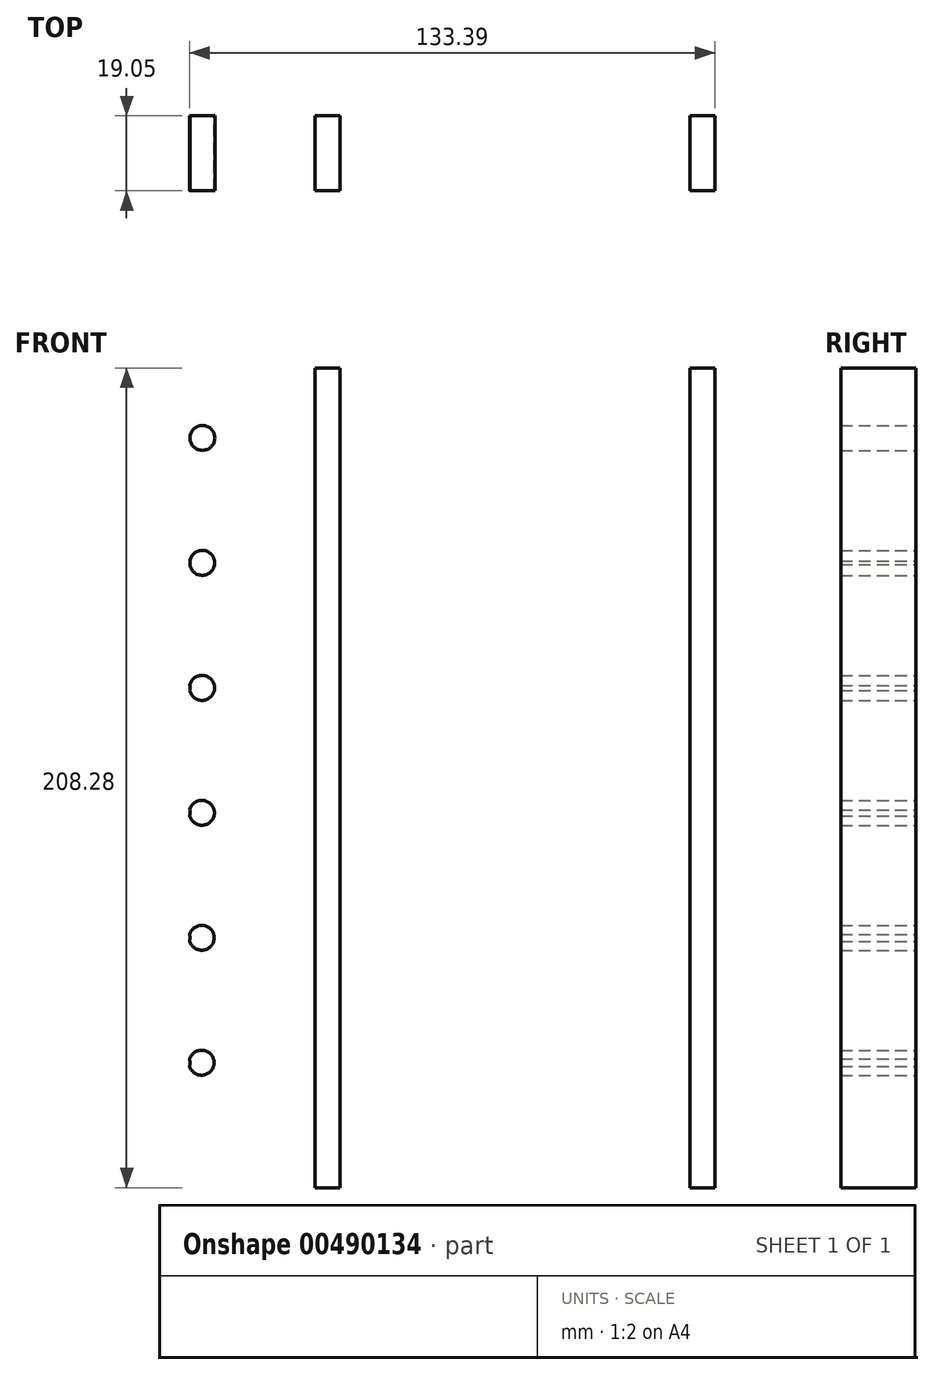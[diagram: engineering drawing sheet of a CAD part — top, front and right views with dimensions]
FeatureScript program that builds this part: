
annotation { "Feature Type Name" : "Feature", "Feature Type Description" : "" }
export const myFeature = defineFeature(function(context is Context, id is Id, definition is map)
    precondition{}
    {
        {
            var Q0;
            Q0=qCreatedBy(makeId("Front.planeOp"),FACE);
            var sketch = newSketch(context, id + "F0", { "sketchPlane" : qUnion([Q0])});
            skCircle(sketch, "E0", {"center": v(63.67, 62.96) * mm, "radius": 12.7 * mm});
            skCircle(sketch, "E1", {"center": v(95.42, 62.96) * mm, "radius": 12.7 * mm});
            skCircle(sketch, "E2", {"center": v(0.17, 62.96) * mm, "radius": 12.7 * mm});
            skCircle(sketch, "E3", {"center": v(31.92, 62.96) * mm, "radius": 12.7 * mm});
            skCircle(sketch, "E4", {"center": v(-31.58, 62.96) * mm, "radius": 12.7 * mm});
            skCircle(sketch, "E5", {"center": v(-63.33, 62.96) * mm, "radius": 12.7 * mm});
            skCircle(sketch, "E6", {"center": v(-95.08, 62.96) * mm, "radius": 12.7 * mm});
            skCircle(sketch, "E7", {"center": v(63.67, -32.3) * mm, "radius": 12.7 * mm});
            skCircle(sketch, "E8", {"center": v(95.42, -32.3) * mm, "radius": 12.7 * mm});
            skCircle(sketch, "E9", {"center": v(0.17, -32.3) * mm, "radius": 12.7 * mm});
            skCircle(sketch, "E10", {"center": v(31.92, -32.3) * mm, "radius": 12.7 * mm});
            skCircle(sketch, "E11", {"center": v(-31.58, -32.3) * mm, "radius": 12.7 * mm});
            skCircle(sketch, "E12", {"center": v(-63.33, -32.3) * mm, "radius": 12.7 * mm});
            skCircle(sketch, "E13", {"center": v(-95.08, -32.3) * mm, "radius": 12.7 * mm});
            skCircle(sketch, "E14", {"center": v(63.67, 31.2) * mm, "radius": 12.7 * mm});
            skCircle(sketch, "E15", {"center": v(95.42, 31.2) * mm, "radius": 12.7 * mm});
            skCircle(sketch, "E16", {"center": v(0.17, 31.2) * mm, "radius": 12.7 * mm});
            skCircle(sketch, "E17", {"center": v(31.92, 31.2) * mm, "radius": 12.7 * mm});
            skCircle(sketch, "E18", {"center": v(-31.58, 31.2) * mm, "radius": 12.7 * mm});
            skCircle(sketch, "E19", {"center": v(-63.33, 31.2) * mm, "radius": 12.7 * mm});
            skCircle(sketch, "E20", {"center": v(-95.08, 31.2) * mm, "radius": 12.7 * mm});
            skCircle(sketch, "E21", {"center": v(63.67, -0.54) * mm, "radius": 12.7 * mm});
            skCircle(sketch, "E22", {"center": v(95.42, -0.54) * mm, "radius": 12.7 * mm});
            skCircle(sketch, "E23", {"center": v(0.17, -0.54) * mm, "radius": 12.7 * mm});
            skCircle(sketch, "E24", {"center": v(31.92, -0.54) * mm, "radius": 12.7 * mm});
            skCircle(sketch, "E25", {"center": v(-31.58, -0.54) * mm, "radius": 12.7 * mm});
            skCircle(sketch, "E26", {"center": v(-63.33, -0.54) * mm, "radius": 12.7 * mm});
            skCircle(sketch, "E27", {"center": v(-95.08, -0.54) * mm, "radius": 12.7 * mm});
            skCircle(sketch, "E28", {"center": v(63.67, -64.04) * mm, "radius": 12.7 * mm});
            skCircle(sketch, "E29", {"center": v(95.42, -64.04) * mm, "radius": 12.7 * mm});
            skCircle(sketch, "E30", {"center": v(0.17, -64.04) * mm, "radius": 12.7 * mm});
            skCircle(sketch, "E31", {"center": v(31.92, -64.04) * mm, "radius": 12.7 * mm});
            skCircle(sketch, "E32", {"center": v(-31.58, -64.04) * mm, "radius": 12.7 * mm});
            skCircle(sketch, "E33", {"center": v(-63.33, -64.04) * mm, "radius": 12.7 * mm});
            skCircle(sketch, "E34", {"center": v(-95.08, -64.04) * mm, "radius": 12.7 * mm});
            skCircle(sketch, "E35", {"center": v(63.67, -95.8) * mm, "radius": 12.7 * mm});
            skCircle(sketch, "E36", {"center": v(95.42, -95.8) * mm, "radius": 12.7 * mm});
            skCircle(sketch, "E37", {"center": v(0.17, -95.8) * mm, "radius": 12.7 * mm});
            skCircle(sketch, "E38", {"center": v(31.92, -95.8) * mm, "radius": 12.7 * mm});
            skCircle(sketch, "E39", {"center": v(-31.58, -95.8) * mm, "radius": 12.7 * mm});
            skCircle(sketch, "E40", {"center": v(-63.33, -95.8) * mm, "radius": 12.7 * mm});
            skCircle(sketch, "E41", {"center": v(-95.08, -95.8) * mm, "radius": 12.7 * mm});
            skLineSegment(sketch, "E42.bottom", {"start": v(-115.4, 82) * mm, "end": v(115.74, 82) * mm});
            skLineSegment(sketch, "E42.top", {"start": v(-115.4, -127.54) * mm, "end": v(115.74, -127.54) * mm});
            skLineSegment(sketch, "E42.left", {"start": v(-115.4, 82) * mm, "end": v(-115.4, -127.54) * mm});
            skLineSegment(sketch, "E42.right", {"start": v(115.74, 82) * mm, "end": v(115.74, -127.54) * mm});
            skLineSegment(sketch, "E43.bottom", {"start": v(-115.4, 82) * mm, "end": v(-107.78, 82) * mm});
            skLineSegment(sketch, "E43.top", {"start": v(-115.4, -127.54) * mm, "end": v(-107.78, -127.54) * mm});
            skLineSegment(sketch, "E43.right", {"start": v(-107.78, 82) * mm, "end": v(-107.78, -127.54) * mm});
            skLineSegment(sketch, "E44.bottom", {"start": v(115.74, 82) * mm, "end": v(108.12, 82) * mm});
            skLineSegment(sketch, "E44.top", {"start": v(115.74, -127.54) * mm, "end": v(108.12, -127.54) * mm});
            skLineSegment(sketch, "E44.right", {"start": v(108.12, 82) * mm, "end": v(108.12, -127.54) * mm});
            skLineSegment(sketch, "E45.top", {"start": v(76.37, -127.54) * mm, "end": v(82.72, -127.54) * mm});
            skLineSegment(sketch, "E46.bottom", {"start": v(44.62, 80.74) * mm, "end": v(50.97, 80.74) * mm});
            skLineSegment(sketch, "E46.top", {"start": v(44.62, -127.54) * mm, "end": v(50.97, -127.54) * mm});
            skLineSegment(sketch, "E46.left", {"start": v(44.62, 80.74) * mm, "end": v(44.62, -127.54) * mm});
            skLineSegment(sketch, "E46.right", {"start": v(50.97, 80.74) * mm, "end": v(50.97, -127.54) * mm});
            skLineSegment(sketch, "E47.bottom", {"start": v(-50.63, 80.74) * mm, "end": v(-44.28, 80.74) * mm});
            skLineSegment(sketch, "E47.top", {"start": v(-50.63, -127.54) * mm, "end": v(-44.28, -127.54) * mm});
            skLineSegment(sketch, "E47.left", {"start": v(-50.63, 80.74) * mm, "end": v(-50.63, -127.54) * mm});
            skLineSegment(sketch, "E47.right", {"start": v(-44.28, 80.74) * mm, "end": v(-44.28, -127.54) * mm});
            skCircle(sketch, "E48", {"center": v(-79.2, 62.96) * mm, "radius": 3.18 * mm});
            skCircle(sketch, "E49.1.0.0", {"center": v(-79.25, 31.2) * mm, "radius": 3.18 * mm});
            skCircle(sketch, "E49.2.0.0", {"center": v(-79.29, -0.54) * mm, "radius": 3.18 * mm});
            skCircle(sketch, "E49.3.0.0", {"center": v(-79.33, -32.3) * mm, "radius": 3.18 * mm});
            skCircle(sketch, "E49.4.0.0", {"center": v(-79.37, -64.04) * mm, "radius": 3.18 * mm});
            skCircle(sketch, "E49.5.0.0", {"center": v(-79.4, -95.8) * mm, "radius": 3.18 * mm});
            skLineSegment(sketch, "E49.direction1", {"start": v(-79.2, 62.96) * mm, "end": v(-79.25, 31.2) * mm, "construction": true});
            skSolve(sketch);
        }
        {
            var Q0;
            {var subQ1=sQuery(id+"F0.wireOp",EDGE,"E44.bottom");Q0=makeQuery(id+"F0.imprint","IMPRINT",FACE,{"disambiguationData":[TD([[makeQuery(id+"F0.imprint","IMPRINT",EDGE,{"derivedFrom":subQ1}),1.0]])]});}
            var Q1;
            {var subQ1=sQuery(id+"F0.wireOp",EDGE,"E46.bottom");Q1=makeQuery(id+"F0.imprint","IMPRINT",FACE,{"disambiguationData":[TD([[makeQuery(id+"F0.imprint","IMPRINT",EDGE,{"derivedFrom":subQ1}),-1.0]])]});}
            var Q2;
            {var subQ1=sQuery(id+"F0.wireOp",EDGE,"E47.bottom");Q2=makeQuery(id+"F0.imprint","IMPRINT",FACE,{"disambiguationData":[TD([[makeQuery(id+"F0.imprint","IMPRINT",EDGE,{"derivedFrom":subQ1}),-1.0]])]});}
            var Q3;
            {var subQ1=sQuery(id+"F0.wireOp",EDGE,"E43.bottom");Q3=makeQuery(id+"F0.imprint","IMPRINT",FACE,{"disambiguationData":[TD([[makeQuery(id+"F0.imprint","IMPRINT",EDGE,{"derivedFrom":subQ1}),-1.0]])]});}
            var Q4;
            {var subQ0=sQuery(id+"F0.wireOp",EDGE,"E49.5.0.0");var subQ1=sQuery(id+"F0.wireOp",EDGE,"E41");var subQ2=makeQuery(id+"F0.imprint","INTERSECT",VERTEX,{"disambiguationData":[OD(0.0)],"derivedFrom":[subQ1,subQ0]});Q4=makeQuery(id+"F0.imprint","IMPRINT",FACE,{"disambiguationData":[TD([[makeQuery(id+"F0.imprint","IMPRINT",EDGE,{"disambiguationData":[TD([[subQ2,1.0]])],"derivedFrom":subQ1}),-1.0]])]});}
            var Q5;
            {var subQ0=sQuery(id+"F0.wireOp",EDGE,"E49.4.0.0");var subQ1=sQuery(id+"F0.wireOp",EDGE,"E34");var subQ2=makeQuery(id+"F0.imprint","INTERSECT",VERTEX,{"disambiguationData":[OD(0.0)],"derivedFrom":[subQ1,subQ0]});Q5=makeQuery(id+"F0.imprint","IMPRINT",FACE,{"disambiguationData":[TD([[makeQuery(id+"F0.imprint","IMPRINT",EDGE,{"disambiguationData":[TD([[subQ2,1.0]])],"derivedFrom":subQ1}),-1.0]])]});}
            var Q6;
            {var subQ0=sQuery(id+"F0.wireOp",EDGE,"E49.3.0.0");var subQ1=sQuery(id+"F0.wireOp",EDGE,"E13");var subQ2=makeQuery(id+"F0.imprint","INTERSECT",VERTEX,{"disambiguationData":[OD(0.0)],"derivedFrom":[subQ1,subQ0]});Q6=makeQuery(id+"F0.imprint","IMPRINT",FACE,{"disambiguationData":[TD([[makeQuery(id+"F0.imprint","IMPRINT",EDGE,{"disambiguationData":[TD([[subQ2,1.0]])],"derivedFrom":subQ1}),-1.0]])]});}
            var Q7;
            {var subQ0=sQuery(id+"F0.wireOp",EDGE,"E49.2.0.0");var subQ1=sQuery(id+"F0.wireOp",EDGE,"E27");var subQ2=makeQuery(id+"F0.imprint","INTERSECT",VERTEX,{"disambiguationData":[OD(0.0)],"derivedFrom":[subQ1,subQ0]});Q7=makeQuery(id+"F0.imprint","IMPRINT",FACE,{"disambiguationData":[TD([[makeQuery(id+"F0.imprint","IMPRINT",EDGE,{"disambiguationData":[TD([[subQ2,1.0]])],"derivedFrom":subQ1}),-1.0]])]});}
            var Q8;
            {var subQ0=sQuery(id+"F0.wireOp",EDGE,"E49.1.0.0");var subQ1=sQuery(id+"F0.wireOp",EDGE,"E20");var subQ2=makeQuery(id+"F0.imprint","INTERSECT",VERTEX,{"disambiguationData":[OD(0.0)],"derivedFrom":[subQ1,subQ0]});Q8=makeQuery(id+"F0.imprint","IMPRINT",FACE,{"disambiguationData":[TD([[makeQuery(id+"F0.imprint","IMPRINT",EDGE,{"disambiguationData":[TD([[subQ2,1.0]])],"derivedFrom":subQ1}),-1.0]])]});}
            var Q9;
            {var subQ0=sQuery(id+"F0.wireOp",EDGE,"E48");var subQ1=makeQuery(id+"F0.imprint","INTERSECT",VERTEX,{"derivedFrom":[sQuery(id+"F0.wireOp",EDGE,"E5"),subQ0]});Q9=makeQuery(id+"F0.imprint","IMPRINT",FACE,{"disambiguationData":[TD([[makeQuery(id+"F0.imprint","IMPRINT",EDGE,{"disambiguationData":[TD([[subQ1,-1.0]])],"derivedFrom":subQ0}),1.0]])]});}
            extrude(context, id + "F1", {"entities" : qUnion([Q0, Q1, Q2, Q3, Q4, Q5, Q6, Q7, Q8, Q9]), "depth" : 19.05 * mm});
        }
    });
